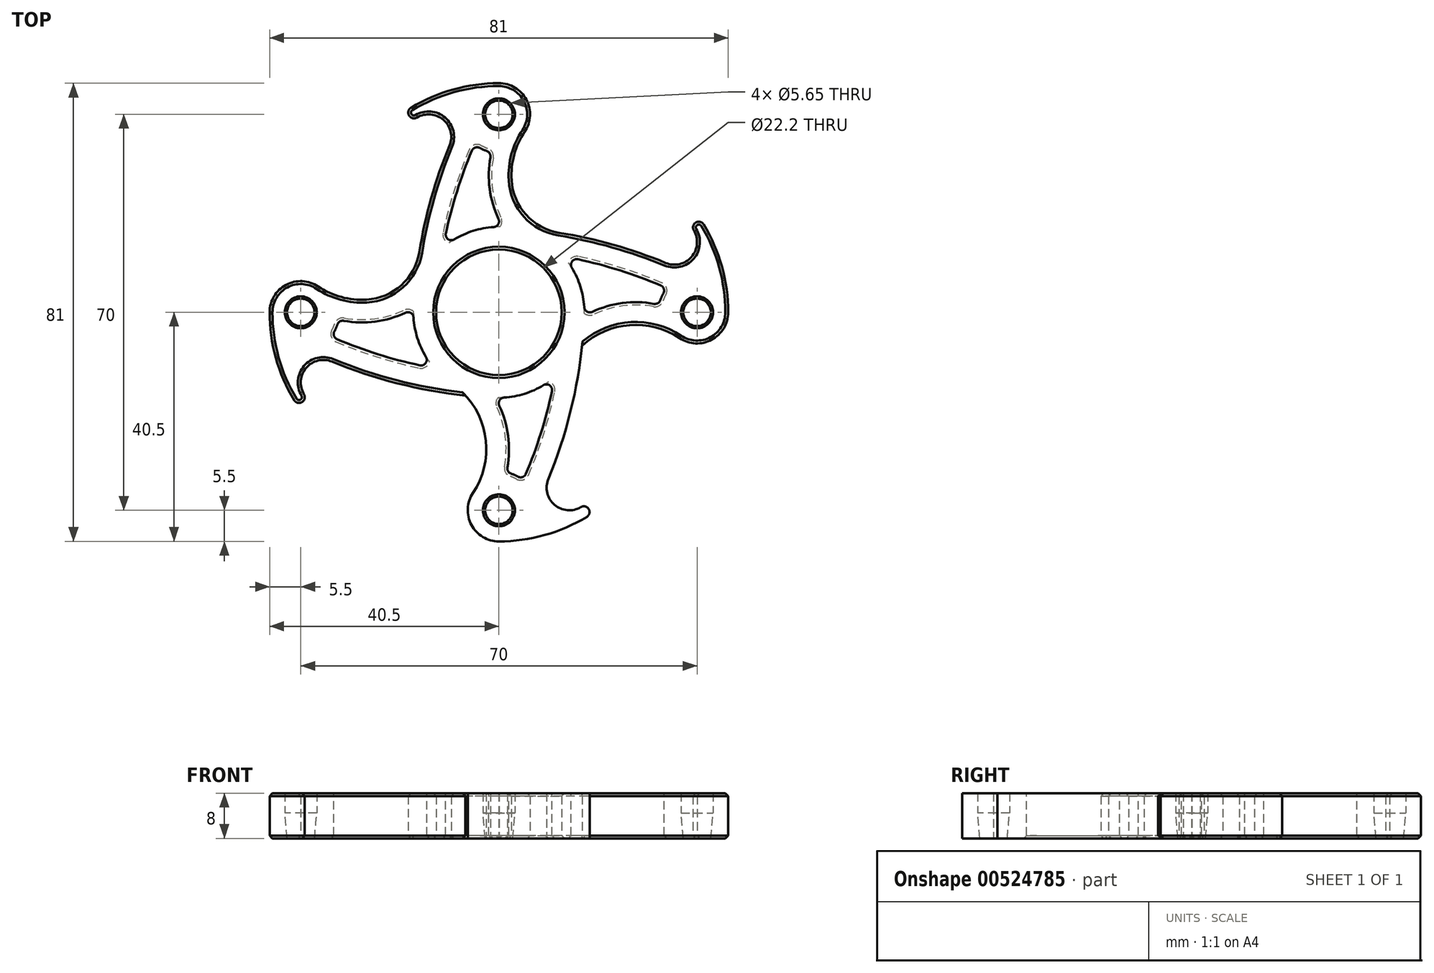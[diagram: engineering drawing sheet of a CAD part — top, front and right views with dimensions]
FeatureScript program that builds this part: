
annotation { "Feature Type Name" : "Feature", "Feature Type Description" : "" }
export const myFeature = defineFeature(function(context is Context, id is Id, definition is map)
    precondition{}
    {
        {
            var Q0;
            Q0=qCreatedBy(makeId("Top.planeOp"),FACE);
            var sketch = newSketch(context, id + "F0", { "sketchPlane" : qUnion([Q0])});
            skCircle(sketch, "E0", {"center": v(0, 0) * mm, "radius": 11.1 * mm});
            skArc(sketch, "E1.0", {"start": v(0.65, 15.09) * mm, "mid": v(-13.47, -6.82) * mm, "end": v(12.54, -8.41) * mm});
            skLineSegment(sketch, "E2", {"start": v(0, 0) * mm, "end": v(35, 0) * mm, "construction": true});
            skArc(sketch, "E3", {"start": v(31.94, -4.57) * mm, "mid": v(37.6, -4.85) * mm, "end": v(40.5, 0) * mm});
            skArc(sketch, "E4", {"start": v(31.94, -4.57) * mm, "mid": v(21.45, -2.48) * mm, "end": v(12.54, -8.41) * mm});
            skArc(sketch, "E5", {"start": v(29.47, 8.72) * mm, "mid": v(15.34, 13.16) * mm, "end": v(0.65, 15.09) * mm});
            skArc(sketch, "E6", {"start": v(29.47, 8.72) * mm, "mid": v(34.28, 10.13) * mm, "end": v(33.95, 15.12) * mm});
            skArc(sketch, "E7", {"start": v(40.5, 0) * mm, "mid": v(39.23, 8.65) * mm, "end": v(35.51, 16.56) * mm});
            skLineSegment(sketch, "E8", {"start": v(31, 12.42) * mm, "end": v(29.47, 8.72) * mm, "construction": true});
            skLineSegment(sketch, "E9", {"start": v(33.95, 15.12) * mm, "end": v(35.51, 16.56) * mm});
            skLineSegment(sketch, "E10", {"start": v(31, 12.42) * mm, "end": v(35.51, 16.56) * mm, "construction": true});
            skSolve(sketch);
        }
        {
            var Q0;
            Q0=makeQuery(id+"F0.imprint","IMPRINT",FACE,{"disambiguationData":[TD([[makeQuery(id+"F0.imprint","IMPRINT",EDGE,{"derivedFrom":sQuery(id+"F0.wireOp",EDGE,"E0")}),-1.0]])]});
            extrude(context, id + "F1", {"entities" : qUnion([Q0]), "endBound" : BoundingType.SYMMETRIC, "depth" : 8 * mm, "offsetDistance" : 25 * mm});
        }
        {
            var Q0;
            Q0=qCreatedBy(makeId("Front.planeOp"),FACE);
            var sketch = newSketch(context, id + "F2", { "sketchPlane" : qUnion([Q0])});
            skLineSegment(sketch, "E11", {"start": v(35, 5.95) * mm, "end": v(35, -6.38) * mm, "construction": true});
            skLineSegment(sketch, "E12", {"start": v(35, 4) * mm, "end": v(37.83, 4) * mm});
            skLineSegment(sketch, "E13", {"start": v(37.83, 4) * mm, "end": v(37.83, 0.5) * mm});
            skLineSegment(sketch, "E14", {"start": v(37.83, 0.5) * mm, "end": v(37.43, -4) * mm});
            skLineSegment(sketch, "E15", {"start": v(37.43, -4) * mm, "end": v(35, -4) * mm});
            skLineSegment(sketch, "E16", {"start": v(35, -4) * mm, "end": v(35, 4) * mm});
            skSolve(sketch);
        }
        {
            var Q0;
            Q0=qSketchRegion(id+"F2",true);
            var Q1;
            Q1=sQuery(id+"F2.wireOp",EDGE,"E11");
            revolve(context, id + "F3", {"operationType" : NewBodyOperationType.REMOVE, "entities" : qUnion([Q0]), "axis" : qUnion([Q1]), "revolveType" : RevolveType.FULL, "oppositeDirection" : true});
        }
        {
            var Q0;
            Q0=makeQuery(id+"F1.opExtrude","CAP_FACE",FACE,{"disambiguationData":[OSD([sQuery(id+"F0.wireOp",EDGE,"E0"),sQuery(id+"F0.wireOp",EDGE,"E1.0"),sQuery(id+"F0.wireOp",EDGE,"E3"),sQuery(id+"F0.wireOp",EDGE,"E4"),sQuery(id+"F0.wireOp",EDGE,"E5")])],"isStart":false});
            var sketch = newSketch(context, id + "F4", { "sketchPlane" : qUnion([Q0])});
            skArc(sketch, "E17.0", {"start": v(15.09, -0.67) * mm, "mid": v(21.5, 1.59) * mm, "end": v(28.3, 1.3) * mm});
            skArc(sketch, "E17.2", {"start": v(29.68, 4.28) * mm, "mid": v(20.72, 7.62) * mm, "end": v(11.43, 9.87) * mm});
            skArc(sketch, "E18.0", {"start": v(15.09, -0.67) * mm, "mid": v(14.27, 4.95) * mm, "end": v(11.43, 9.87) * mm});
            skArc(sketch, "E19.0", {"start": v(29.68, 4.28) * mm, "mid": v(28.81, 2.88) * mm, "end": v(28.3, 1.3) * mm});
            skSolve(sketch);
        }
        {
            var Q0;
            Q0=qSketchRegion(id+"F4",true);
            extrude(context, id + "F5", {"entities" : qUnion([Q0]), "operationType" : NewBodyOperationType.REMOVE, "oppositeDirection" : true, "depth" : 25 * mm, "offsetDistance" : 25 * mm});
        }
        {
            var Q0;
            Q0=makeQuery(id+"F5.boolean.opBoolean","COPY",EDGE,{"derivedFrom":makeQuery(id+"F5.opExtrude","SWEPT_EDGE",EDGE,{"disambiguationData":[OSD([sQuery(id+"F4.wireOp",EDGE,"E17.0"),sQuery(id+"F4.wireOp",EDGE,"E18.0")])]})});
            var Q1;
            Q1=makeQuery(id+"F5.boolean.opBoolean","COPY",EDGE,{"derivedFrom":makeQuery(id+"F5.opExtrude","SWEPT_EDGE",EDGE,{"disambiguationData":[OSD([sQuery(id+"F4.wireOp",EDGE,"E17.2"),sQuery(id+"F4.wireOp",EDGE,"E18.0")])]})});
            var Q2;
            Q2=makeQuery(id+"F5.boolean.opBoolean","COPY",EDGE,{"derivedFrom":makeQuery(id+"F5.opExtrude","SWEPT_EDGE",EDGE,{"disambiguationData":[OSD([sQuery(id+"F4.wireOp",EDGE,"E17.0"),sQuery(id+"F4.wireOp",EDGE,"E19.0")])]})});
            var Q3;
            Q3=makeQuery(id+"F5.boolean.opBoolean","COPY",EDGE,{"derivedFrom":makeQuery(id+"F5.opExtrude","SWEPT_EDGE",EDGE,{"disambiguationData":[OSD([sQuery(id+"F4.wireOp",EDGE,"E17.2"),sQuery(id+"F4.wireOp",EDGE,"E19.0")])]})});
            var Q4;
            Q4=makeQuery(id+"F1.opExtrude","SWEPT_EDGE",EDGE,{"disambiguationData":[OSD([sQuery(id+"F0.wireOp",EDGE,"E6"),sQuery(id+"F0.wireOp",EDGE,"E9")])]});
            var Q5;
            Q5=makeQuery(id+"F1.opExtrude","SWEPT_EDGE",EDGE,{"disambiguationData":[OSD([sQuery(id+"F0.wireOp",EDGE,"E7"),sQuery(id+"F0.wireOp",EDGE,"E9")])]});
            fillet(context, id + "F6", {"entities" : qUnion([Q0, Q1, Q2, Q3, Q4, Q5]), "radius" : 1 * mm, "tangentPropagation" : true, "allowEdgeOverflow" : false});
        }
        {
            var Q0;
            Q0=makeQuery(id+"F5.boolean.opBoolean","COPY",EDGE,{"derivedFrom":makeQuery(id+"F5.opExtrude","CAP_EDGE",EDGE,{"disambiguationData":[OSD([sQuery(id+"F4.wireOp",EDGE,"E17.0")])],"isStart":true})});
            var Q1;
            Q1=makeQuery(id+"F5.boolean.opBoolean","COPY",EDGE,{"derivedFrom":makeQuery(id+"F5.opExtrude","CAP_EDGE",EDGE,{"disambiguationData":[OSD([sQuery(id+"F4.wireOp",EDGE,"E18.0")])],"isStart":true})});
            var Q2;
            Q2=makeQuery(id+"F5.boolean.opBoolean","COPY",EDGE,{"derivedFrom":makeQuery(id+"F5.opExtrude","CAP_EDGE",EDGE,{"disambiguationData":[OSD([sQuery(id+"F4.wireOp",EDGE,"E17.2")])],"isStart":true})});
            var Q3;
            Q3=makeQuery(id+"F5.boolean.opBoolean","COPY",EDGE,{"derivedFrom":makeQuery(id+"F5.opExtrude","CAP_EDGE",EDGE,{"disambiguationData":[OSD([sQuery(id+"F4.wireOp",EDGE,"E19.0")])],"isStart":true})});
            var Q4;
            Q4=makeQuery(id+"F1.opExtrude","CAP_EDGE",EDGE,{"disambiguationData":[OSD([sQuery(id+"F0.wireOp",EDGE,"E0")])],"isStart":false});
            var Q5;
            Q5=makeQuery(id+"F5.boolean.opBoolean","INTERSECT",EDGE,{"derivedFrom":[makeQuery(id+"F1.opExtrude","CAP_FACE",FACE,{"disambiguationData":[OSD([sQuery(id+"F0.wireOp",EDGE,"E0"),sQuery(id+"F0.wireOp",EDGE,"E1.0"),sQuery(id+"F0.wireOp",EDGE,"E3"),sQuery(id+"F0.wireOp",EDGE,"E4"),sQuery(id+"F0.wireOp",EDGE,"E5")])],"isStart":true}),makeQuery(id+"F5.opExtrude","SWEPT_FACE",FACE,{"disambiguationData":[OSD([sQuery(id+"F4.wireOp",EDGE,"E17.2")])]})]});
            var Q6;
            Q6=makeQuery(id+"F5.boolean.opBoolean","INTERSECT",EDGE,{"derivedFrom":[makeQuery(id+"F1.opExtrude","CAP_FACE",FACE,{"disambiguationData":[OSD([sQuery(id+"F0.wireOp",EDGE,"E0"),sQuery(id+"F0.wireOp",EDGE,"E1.0"),sQuery(id+"F0.wireOp",EDGE,"E3"),sQuery(id+"F0.wireOp",EDGE,"E4"),sQuery(id+"F0.wireOp",EDGE,"E5")])],"isStart":true}),makeQuery(id+"F5.opExtrude","SWEPT_FACE",FACE,{"disambiguationData":[OSD([sQuery(id+"F4.wireOp",EDGE,"E17.0")])]})]});
            var Q7;
            Q7=makeQuery(id+"F5.boolean.opBoolean","INTERSECT",EDGE,{"derivedFrom":[makeQuery(id+"F1.opExtrude","CAP_FACE",FACE,{"disambiguationData":[OSD([sQuery(id+"F0.wireOp",EDGE,"E0"),sQuery(id+"F0.wireOp",EDGE,"E1.0"),sQuery(id+"F0.wireOp",EDGE,"E3"),sQuery(id+"F0.wireOp",EDGE,"E4"),sQuery(id+"F0.wireOp",EDGE,"E5")])],"isStart":true}),makeQuery(id+"F5.opExtrude","SWEPT_FACE",FACE,{"disambiguationData":[OSD([sQuery(id+"F4.wireOp",EDGE,"E19.0")])]})]});
            var Q8;
            Q8=makeQuery(id+"F1.opExtrude","CAP_EDGE",EDGE,{"disambiguationData":[OSD([sQuery(id+"F0.wireOp",EDGE,"E0")])],"isStart":true});
            var Q9;
            Q9=makeQuery(id+"F5.boolean.opBoolean","INTERSECT",EDGE,{"derivedFrom":[makeQuery(id+"F1.opExtrude","CAP_FACE",FACE,{"disambiguationData":[OSD([sQuery(id+"F0.wireOp",EDGE,"E0"),sQuery(id+"F0.wireOp",EDGE,"E1.0"),sQuery(id+"F0.wireOp",EDGE,"E3"),sQuery(id+"F0.wireOp",EDGE,"E4"),sQuery(id+"F0.wireOp",EDGE,"E5")])],"isStart":true}),makeQuery(id+"F5.opExtrude","SWEPT_FACE",FACE,{"disambiguationData":[OSD([sQuery(id+"F4.wireOp",EDGE,"E18.0")])]})]});
            var Q10;
            Q10=makeQuery(id+"F3.boolean.opBoolean","COPY",EDGE,{"derivedFrom":makeQuery(id+"F3.opRevolve","SWEPT_EDGE",EDGE,{"disambiguationData":[OSD([sQuery(id+"F2.wireOp",EDGE,"E12"),sQuery(id+"F2.wireOp",EDGE,"E13")])]})});
            chamfer(context, id + "F7", {"entities" : qUnion([Q0, Q1, Q2, Q3, Q4, Q5, Q6, Q7, Q8, Q9, Q10]), "width" : .5 * mm, "tangentPropagation" : true});
        }
        {
            var Q0;
            Q0=makeQuery(id+"F1.opExtrude","SWEPT_BODY",BODY,{"disambiguationData":[OSD([sQuery(id+"F0.wireOp",EDGE,"E0"),sQuery(id+"F0.wireOp",EDGE,"E1.0"),sQuery(id+"F0.wireOp",EDGE,"E3"),sQuery(id+"F0.wireOp",EDGE,"E4"),sQuery(id+"F0.wireOp",EDGE,"E5")])]});
            var Q1;
            Q1=makeQuery(id+"F1.opExtrude","SWEPT_FACE",FACE,{"disambiguationData":[OSD([sQuery(id+"F0.wireOp",EDGE,"E0")])]});
            circularPattern(context, id + "F8", {"operationType" : NewBodyOperationType.ADD, "entities" : qUnion([Q0]), "axis" : qUnion([Q1]), "angle" : 360 * degree, "instanceCount" : 4, "equalSpace" : true});
        }
        {
            var Q0;
            Q0=makeQuery(id+"F8.boolean.opBoolean","INTERSECT",EDGE,{"derivedFrom":[makeQuery(id+"F1.opExtrude","SWEPT_FACE",FACE,{"disambiguationData":[OSD([sQuery(id+"F0.wireOp",EDGE,"E4")])]}),makeQuery(id+"F8.opPattern","COPY",FACE,{"derivedFrom":makeQuery(id+"F1.opExtrude","SWEPT_FACE",FACE,{"disambiguationData":[OSD([sQuery(id+"F0.wireOp",EDGE,"E5")])]}),"instanceName":"2"})]});
            var Q1;
            Q1=makeQuery(id+"F8.boolean.opBoolean","INTERSECT",EDGE,{"derivedFrom":[makeQuery(id+"F1.opExtrude","SWEPT_FACE",FACE,{"disambiguationData":[OSD([sQuery(id+"F0.wireOp",EDGE,"E5")])]}),makeQuery(id+"F8.opPattern","COPY",FACE,{"derivedFrom":makeQuery(id+"F1.opExtrude","SWEPT_FACE",FACE,{"disambiguationData":[OSD([sQuery(id+"F0.wireOp",EDGE,"E4")])]}),"instanceName":"1"})]});
            var Q2;
            Q2=makeQuery(id+"F8.boolean.opBoolean","INTERSECT",EDGE,{"derivedFrom":[makeQuery(id+"F8.opPattern","COPY",FACE,{"derivedFrom":makeQuery(id+"F1.opExtrude","SWEPT_FACE",FACE,{"disambiguationData":[OSD([sQuery(id+"F0.wireOp",EDGE,"E5")])]}),"instanceName":"1"}),makeQuery(id+"F8.opPattern","COPY",FACE,{"derivedFrom":makeQuery(id+"F1.opExtrude","SWEPT_FACE",FACE,{"disambiguationData":[OSD([sQuery(id+"F0.wireOp",EDGE,"E4")])]}),"instanceName":"2"})]});
            fillet(context, id + "F9", {"entities" : qUnion([Q0, Q1, Q2]), "radius" : 10 * mm, "tangentPropagation" : true, "allowEdgeOverflow" : false});
        }
        {
            var Q0;
            Q0=makeQuery(id+"F1.opExtrude","CAP_EDGE",EDGE,{"disambiguationData":[OSD([sQuery(id+"F0.wireOp",EDGE,"E5")])],"isStart":false});
            var Q1;
            Q1=makeQuery(id+"F1.opExtrude","CAP_EDGE",EDGE,{"disambiguationData":[OSD([sQuery(id+"F0.wireOp",EDGE,"E5")])],"isStart":true});
            chamfer(context, id + "F10", {"entities" : qUnion([Q0, Q1]), "width" : .5 * mm, "tangentPropagation" : true});
        }
    });
